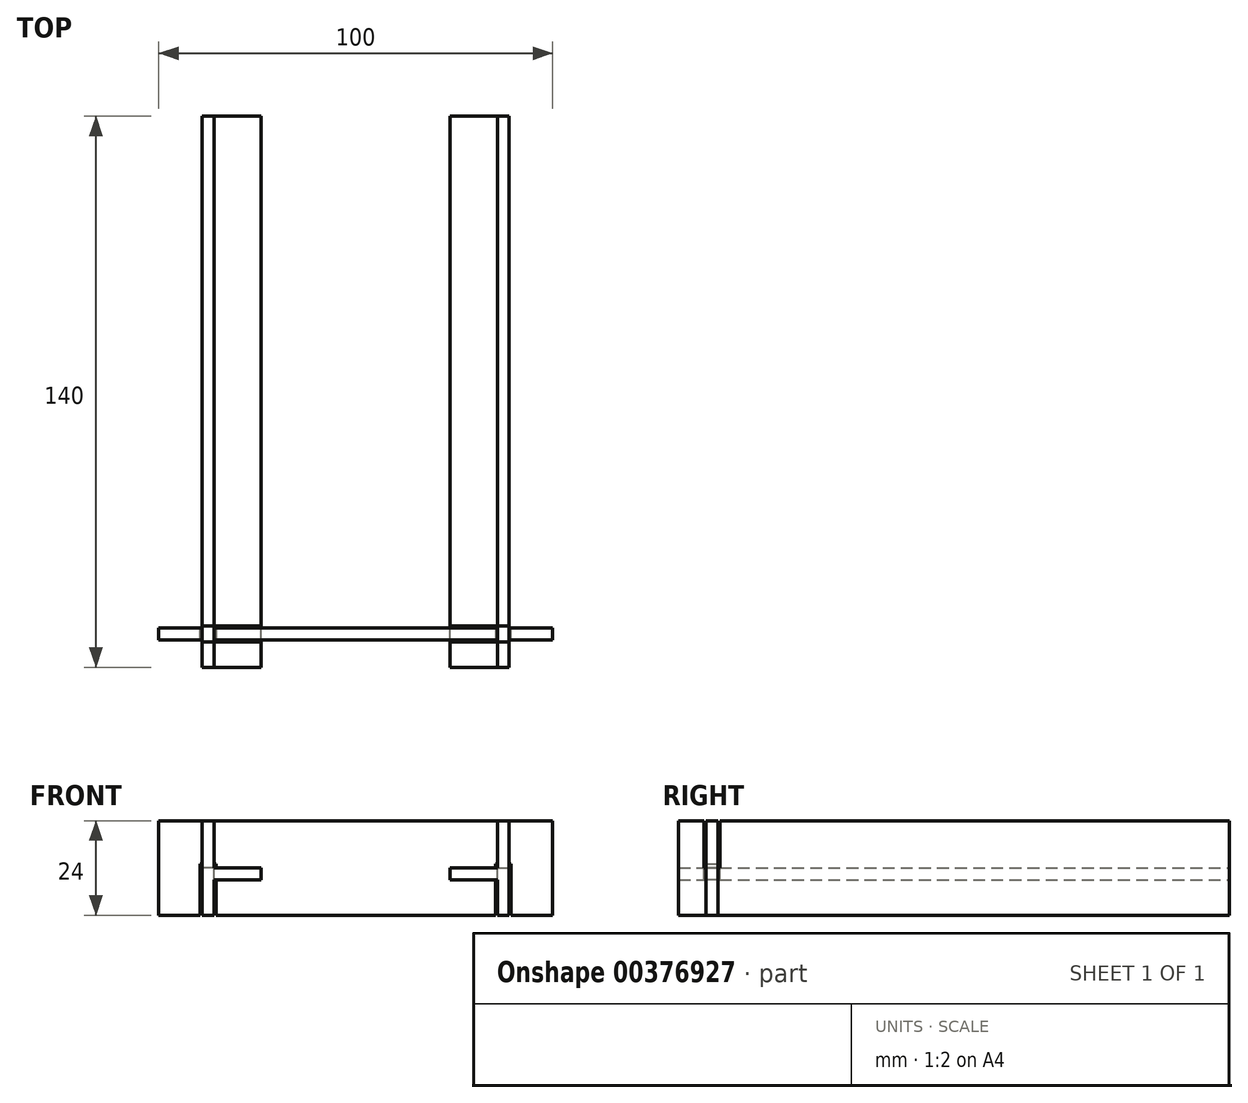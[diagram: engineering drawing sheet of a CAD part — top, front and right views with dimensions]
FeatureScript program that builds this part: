
annotation { "Feature Type Name" : "Feature", "Feature Type Description" : "" }
export const myFeature = defineFeature(function(context is Context, id is Id, definition is map)
    precondition{}
    {
        {
            var Q0;
            Q0=qCreatedBy(makeId("Front.planeOp"),FACE);
            var sketch = newSketch(context, id + "F0", { "sketchPlane" : qUnion([Q0])});
            skLineSegment(sketch, "E0.bottom", {"start": v(36, 0) * mm, "end": v(39, 0) * mm});
            skLineSegment(sketch, "E0.top", {"start": v(36, 24) * mm, "end": v(39, 24) * mm});
            skLineSegment(sketch, "E0.left", {"start": v(36, 0) * mm, "end": v(36, 24) * mm});
            skLineSegment(sketch, "E0.right", {"start": v(39, 0) * mm, "end": v(39, 24) * mm});
            skLineSegment(sketch, "E1.bottom", {"start": v(36, 12) * mm, "end": v(24, 12) * mm});
            skLineSegment(sketch, "E1.top", {"start": v(36, 9) * mm, "end": v(24, 9) * mm});
            skLineSegment(sketch, "E1.left", {"start": v(36, 12) * mm, "end": v(36, 9) * mm});
            skLineSegment(sketch, "E1.right", {"start": v(24, 12) * mm, "end": v(24, 9) * mm});
            skSolve(sketch);
        }
        {
            var Q0;
            Q0 = qSketchRegion(id + "F0", true);
            extrude(context, id + "F1", {"entities" : qUnion([Q0]), "depth" : 70 * mm, "hasSecondDirection" : true, "secondDirectionOppositeDirection" : true, "secondDirectionDepth" : 70 * mm});
        }
        {
            var Q0;
            Q0=makeQuery(id+"F1.opExtrude","SWEPT_BODY",BODY,{"disambiguationData":[OSD([sQuery(id+"F0.wireOp",EDGE,"E0.bottom"),sQuery(id+"F0.wireOp",EDGE,"E0.top"),sQuery(id+"F0.wireOp",EDGE,"E0.left"),sQuery(id+"F0.wireOp",EDGE,"E0.right"),sQuery(id+"F0.wireOp",EDGE,"E1.bottom"),sQuery(id+"F0.wireOp",EDGE,"E1.top"),sQuery(id+"F0.wireOp",EDGE,"E1.right")])]});
            var Q1;
            Q1=qCreatedBy(makeId("Right.planeOp"),FACE);
            mirror(context, id + "F2", {"entities" : qUnion([Q0]), "mirrorPlane" : qUnion([Q1])});
        }
        {
            var Q0;
            Q0=qCreatedBy(makeId("Front.planeOp"),FACE);
            cPlane(context, id + "F3", {"entities" : qUnion([Q0]), "cplaneType" : CPlaneType.OFFSET, "offset" : 60 * mm, "width" : 150 * mm, "height" : 150 * mm});
        }
        {
            var Q0;
            Q0=qCreatedBy(id+"F3.planeOp",FACE);
            var sketch = newSketch(context, id + "F4", { "sketchPlane" : qUnion([Q0])});
            skLineSegment(sketch, "E2.bottom", {"start": v(-50, 0) * mm, "end": v(-39.5, 0) * mm});
            skLineSegment(sketch, "E2.top", {"start": v(-50, 24) * mm, "end": v(50, 24) * mm});
            skLineSegment(sketch, "E2.left", {"start": v(-50, 0) * mm, "end": v(-50, 24) * mm});
            skLineSegment(sketch, "E2.right", {"start": v(50, 0) * mm, "end": v(50, 24) * mm});
            skLineSegment(sketch, "E3.top", {"start": v(-39.5, 13) * mm, "end": v(-35.5, 13) * mm});
            skLineSegment(sketch, "E3.left", {"start": v(-39.5, 0) * mm, "end": v(-39.5, 13) * mm});
            skLineSegment(sketch, "E3.right", {"start": v(-35.5, 0) * mm, "end": v(-35.5, 13) * mm});
            skLineSegment(sketch, "E4.top", {"start": v(35.5, 13) * mm, "end": v(39.5, 13) * mm});
            skLineSegment(sketch, "E4.left", {"start": v(35.5, 0) * mm, "end": v(35.5, 13) * mm});
            skLineSegment(sketch, "E4.right", {"start": v(39.5, 0) * mm, "end": v(39.5, 13) * mm});
            skLineSegment(sketch, "E5.trimOffspring", {"start": v(-35.5, 0) * mm, "end": v(35.5, 0) * mm});
            skLineSegment(sketch, "E6.trimOffspring", {"start": v(39.5, 0) * mm, "end": v(50, 0) * mm});
            skSolve(sketch);
        }
        {
            var Q0;
            Q0 = qSketchRegion(id + "F4", true);
            extrude(context, id + "F5", {"entities" : qUnion([Q0]), "depth" : 3 * mm});
        }
        {
            var Q0;
            Q0=makeQuery(id+"F1.opExtrude","SWEPT_FACE",FACE,{"disambiguationData":[OSD([sQuery(id+"F0.wireOp",EDGE,"E0.right")])]});
            var sketch = newSketch(context, id + "F6", { "sketchPlane" : qUnion([Q0])});
            skLineSegment(sketch, "E7.bottom", {"start": v(-63.5, 24) * mm, "end": v(-59.5, 24) * mm});
            skLineSegment(sketch, "E7.top", {"start": v(-63.5, 12) * mm, "end": v(-59.5, 12) * mm});
            skLineSegment(sketch, "E7.left", {"start": v(-63.5, 24) * mm, "end": v(-63.5, 12) * mm});
            skLineSegment(sketch, "E7.right", {"start": v(-59.5, 24) * mm, "end": v(-59.5, 12) * mm});
            skSolve(sketch);
        }
        {
            var Q0;
            Q0 = qSketchRegion(id + "F6", true);
            var Q1;
            {var subQ0=sQuery(id+"F0.wireOp",EDGE,"E0.left");Q1=makeQuery(id+"F1.opExtrude","SWEPT_FACE",FACE,{"disambiguationData":[OSD([subQ0]),TDD([makeQuery(id+"F0.imprint","IMPRINT",EDGE,{"disambiguationData":[TD([[makeQuery(id+"F0.imprint","INTERSECT",VERTEX,{"derivedFrom":[sQuery(id+"F0.wireOp",EDGE,"E0.top"),subQ0]}),1.0]])],"derivedFrom":subQ0})])]});}
            extrude(context, id + "F7", {"entities" : qUnion([Q0]), "operationType" : NewBodyOperationType.REMOVE, "endBound" : BoundingType.UP_TO_SURFACE, "oppositeDirection" : true, "endBoundEntityFace" : qUnion([Q1]), "depth" : 25 * mm});
        }
        {
            var Q0;
            Q0=makeQuery(id+"F2.opPattern","COPY",FACE,{"derivedFrom":makeQuery(id+"F1.opExtrude","SWEPT_FACE",FACE,{"disambiguationData":[OSD([sQuery(id+"F0.wireOp",EDGE,"E0.right")])]}),"instanceName":"1"});
            var sketch = newSketch(context, id + "F8", { "sketchPlane" : qUnion([Q0])});
            skLineSegment(sketch, "E8.bottom", {"start": v(59.5, 24) * mm, "end": v(63.5, 24) * mm});
            skLineSegment(sketch, "E8.top", {"start": v(59.5, 12) * mm, "end": v(63.5, 12) * mm});
            skLineSegment(sketch, "E8.left", {"start": v(59.5, 24) * mm, "end": v(59.5, 12) * mm});
            skLineSegment(sketch, "E8.right", {"start": v(63.5, 24) * mm, "end": v(63.5, 12) * mm});
            skSolve(sketch);
        }
        {
            var Q0;
            Q0 = qSketchRegion(id + "F8", true);
            var Q1;
            {var subQ0=sQuery(id+"F0.wireOp",EDGE,"E0.left");Q1=makeQuery(id+"F2.opPattern","COPY",FACE,{"derivedFrom":makeQuery(id+"F1.opExtrude","SWEPT_FACE",FACE,{"disambiguationData":[OSD([subQ0]),TDD([makeQuery(id+"F0.imprint","IMPRINT",EDGE,{"disambiguationData":[TD([[makeQuery(id+"F0.imprint","INTERSECT",VERTEX,{"derivedFrom":[sQuery(id+"F0.wireOp",EDGE,"E0.top"),subQ0]}),1.0]])],"derivedFrom":subQ0})])]}),"instanceName":"1"});}
            extrude(context, id + "F9", {"entities" : qUnion([Q0]), "operationType" : NewBodyOperationType.REMOVE, "endBound" : BoundingType.UP_TO_SURFACE, "oppositeDirection" : true, "endBoundEntityFace" : qUnion([Q1]), "depth" : 25 * mm});
        }
        {
            var Q0;
            Q0=makeQuery(id+"F7.boolean.opBoolean","MERGE",FACE,{"derivedFrom":[makeQuery(id+"F1.opExtrude","SWEPT_FACE",FACE,{"disambiguationData":[OSD([sQuery(id+"F0.wireOp",EDGE,"E1.bottom")])]}),makeQuery(id+"F7.opExtrude","SWEPT_FACE",FACE,{"disambiguationData":[OSD([sQuery(id+"F6.wireOp",EDGE,"E7.top")])]})]});
            var sketch = newSketch(context, id + "F10", { "sketchPlane" : qUnion([Q0])});
            skLineSegment(sketch, "E9.bottom", {"start": v(24, -59.5) * mm, "end": v(36, -59.5) * mm});
            skLineSegment(sketch, "E9.top", {"start": v(24, -63.5) * mm, "end": v(36, -63.5) * mm});
            skLineSegment(sketch, "E9.left", {"start": v(24, -59.5) * mm, "end": v(24, -63.5) * mm});
            skLineSegment(sketch, "E9.right", {"start": v(36, -59.5) * mm, "end": v(36, -63.5) * mm});
            skSolve(sketch);
        }
        {
            var Q0;
            Q0 = qSketchRegion(id + "F10", true);
            var Q1;
            Q1=makeQuery(id+"F1.opExtrude","SWEPT_FACE",FACE,{"disambiguationData":[OSD([sQuery(id+"F0.wireOp",EDGE,"E1.top")])]});
            extrude(context, id + "F11", {"entities" : qUnion([Q0]), "operationType" : NewBodyOperationType.REMOVE, "endBound" : BoundingType.UP_TO_SURFACE, "oppositeDirection" : true, "endBoundEntityFace" : qUnion([Q1]), "depth" : 25 * mm});
        }
        {
            var Q0;
            Q0=makeQuery(id+"F9.boolean.opBoolean","MERGE",FACE,{"derivedFrom":[makeQuery(id+"F2.opPattern","COPY",FACE,{"derivedFrom":makeQuery(id+"F1.opExtrude","SWEPT_FACE",FACE,{"disambiguationData":[OSD([sQuery(id+"F0.wireOp",EDGE,"E1.bottom")])]}),"instanceName":"1"}),makeQuery(id+"F9.opExtrude","SWEPT_FACE",FACE,{"disambiguationData":[OSD([sQuery(id+"F8.wireOp",EDGE,"E8.top")])]})]});
            var sketch = newSketch(context, id + "F12", { "sketchPlane" : qUnion([Q0])});
            skLineSegment(sketch, "E10.bottom", {"start": v(-36, -63.5) * mm, "end": v(-24, -63.5) * mm});
            skLineSegment(sketch, "E10.top", {"start": v(-36, -59.5) * mm, "end": v(-24, -59.5) * mm});
            skLineSegment(sketch, "E10.left", {"start": v(-36, -63.5) * mm, "end": v(-36, -59.5) * mm});
            skLineSegment(sketch, "E10.right", {"start": v(-24, -63.5) * mm, "end": v(-24, -59.5) * mm});
            skSolve(sketch);
        }
        {
            var Q0;
            Q0 = qSketchRegion(id + "F12", true);
            var Q1;
            Q1=makeQuery(id+"F2.opPattern","COPY",FACE,{"derivedFrom":makeQuery(id+"F1.opExtrude","SWEPT_FACE",FACE,{"disambiguationData":[OSD([sQuery(id+"F0.wireOp",EDGE,"E1.top")])]}),"instanceName":"1"});
            extrude(context, id + "F13", {"entities" : qUnion([Q0]), "operationType" : NewBodyOperationType.REMOVE, "endBound" : BoundingType.UP_TO_SURFACE, "oppositeDirection" : true, "endBoundEntityFace" : qUnion([Q1]), "depth" : 25 * mm});
        }
    });
